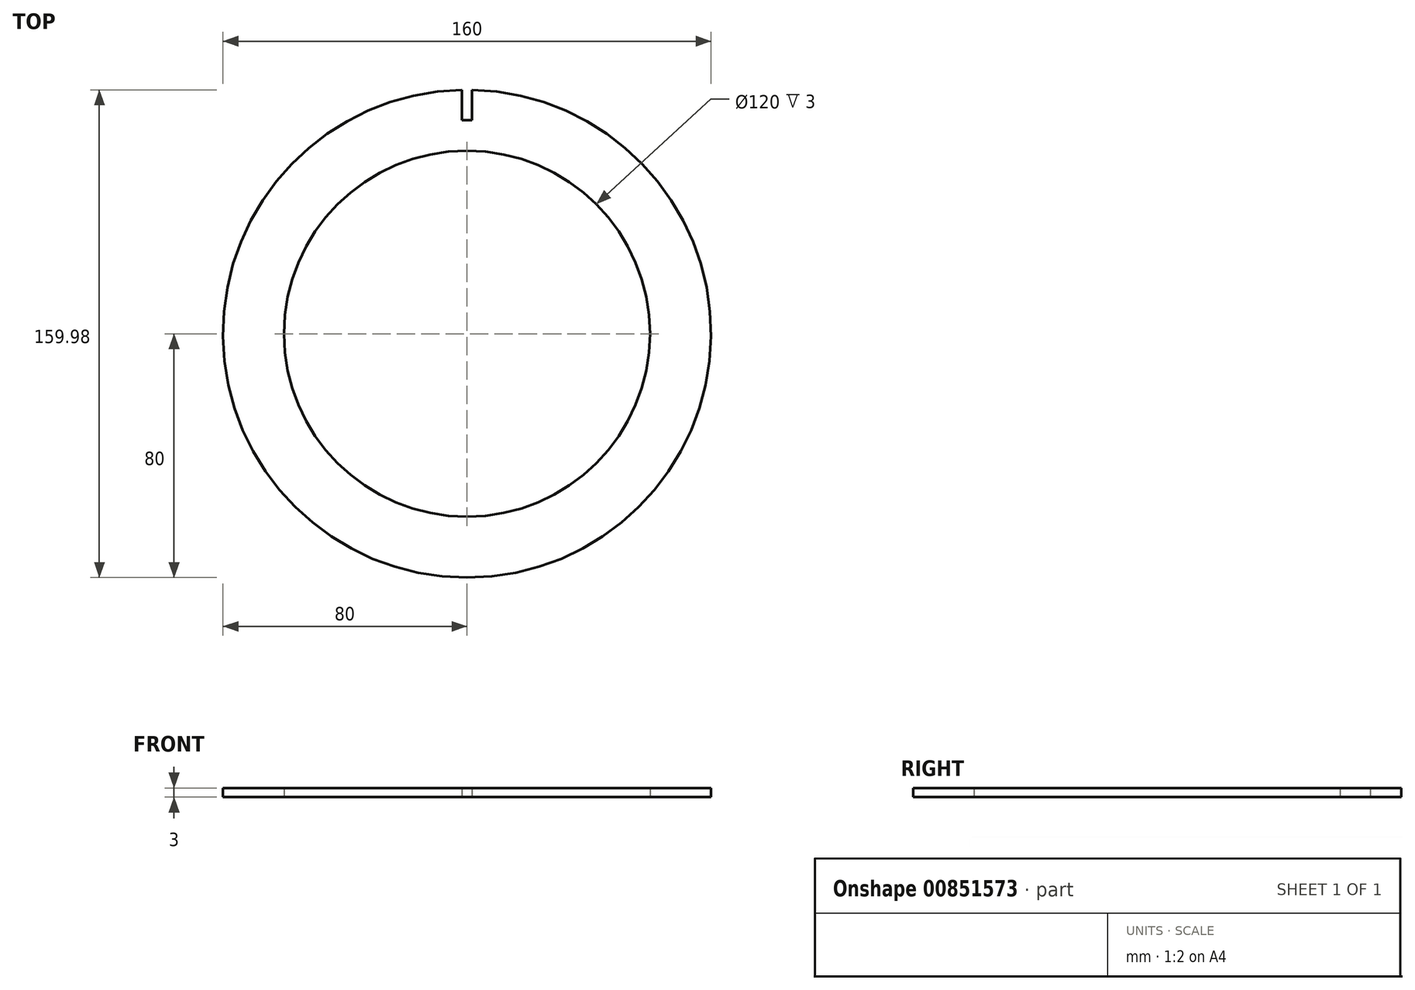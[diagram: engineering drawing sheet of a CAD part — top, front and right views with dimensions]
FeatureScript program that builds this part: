
annotation { "Feature Type Name" : "Feature", "Feature Type Description" : "" }
export const myFeature = defineFeature(function(context is Context, id is Id, definition is map)
    precondition{}
    {
        {
            var Q0;
            Q0=qCreatedBy(makeId("Top.planeOp"),FACE);
            var sketch = newSketch(context, id + "F0", { "sketchPlane" : qUnion([Q0])});
            skCircle(sketch, "E0", {"center": v(0, 0) * mm, "radius": 80 * mm});
            skCircle(sketch, "E1", {"center": v(0, 0) * mm, "radius": 60 * mm});
            skSolve(sketch);
        }
        {
            var Q0;
            Q0=makeQuery(id+"F0.imprint","IMPRINT",FACE,{"disambiguationData":[TD([[makeQuery(id+"F0.imprint","IMPRINT",EDGE,{"derivedFrom":sQuery(id+"F0.wireOp",EDGE,"E0")}),1.0]])]});
            extrude(context, id + "F1", {"entities" : qUnion([Q0]), "depth" : 3 * mm, "offsetDistance" : 25 * mm});
        }
        {
            var Q0;
            Q0=makeQuery(id+"F1.opExtrude","CAP_FACE",FACE,{"disambiguationData":[OSD([sQuery(id+"F0.wireOp",EDGE,"E0"),sQuery(id+"F0.wireOp",EDGE,"E1")])],"isStart":false});
            var sketch = newSketch(context, id + "F2", { "sketchPlane" : qUnion([Q0])});
            skLineSegment(sketch, "E2.bottom", {"start": v(-1.6, 80) * mm, "end": v(1.6, 80) * mm});
            skLineSegment(sketch, "E2.top", {"start": v(-1.6, 70) * mm, "end": v(1.6, 70) * mm});
            skLineSegment(sketch, "E2.left", {"start": v(-1.6, 80) * mm, "end": v(-1.6, 70) * mm});
            skLineSegment(sketch, "E2.right", {"start": v(1.6, 80) * mm, "end": v(1.6, 70) * mm});
            skLineSegment(sketch, "E3", {"start": v(0, 0) * mm, "end": v(0, 70) * mm, "construction": true});
            skSolve(sketch);
        }
        {
            var Q0;
            Q0=qSketchRegion(id+"F2",true);
            extrude(context, id + "F3", {"entities" : qUnion([Q0]), "operationType" : NewBodyOperationType.REMOVE, "oppositeDirection" : true, "depth" : 25 * mm});
        }
    });
